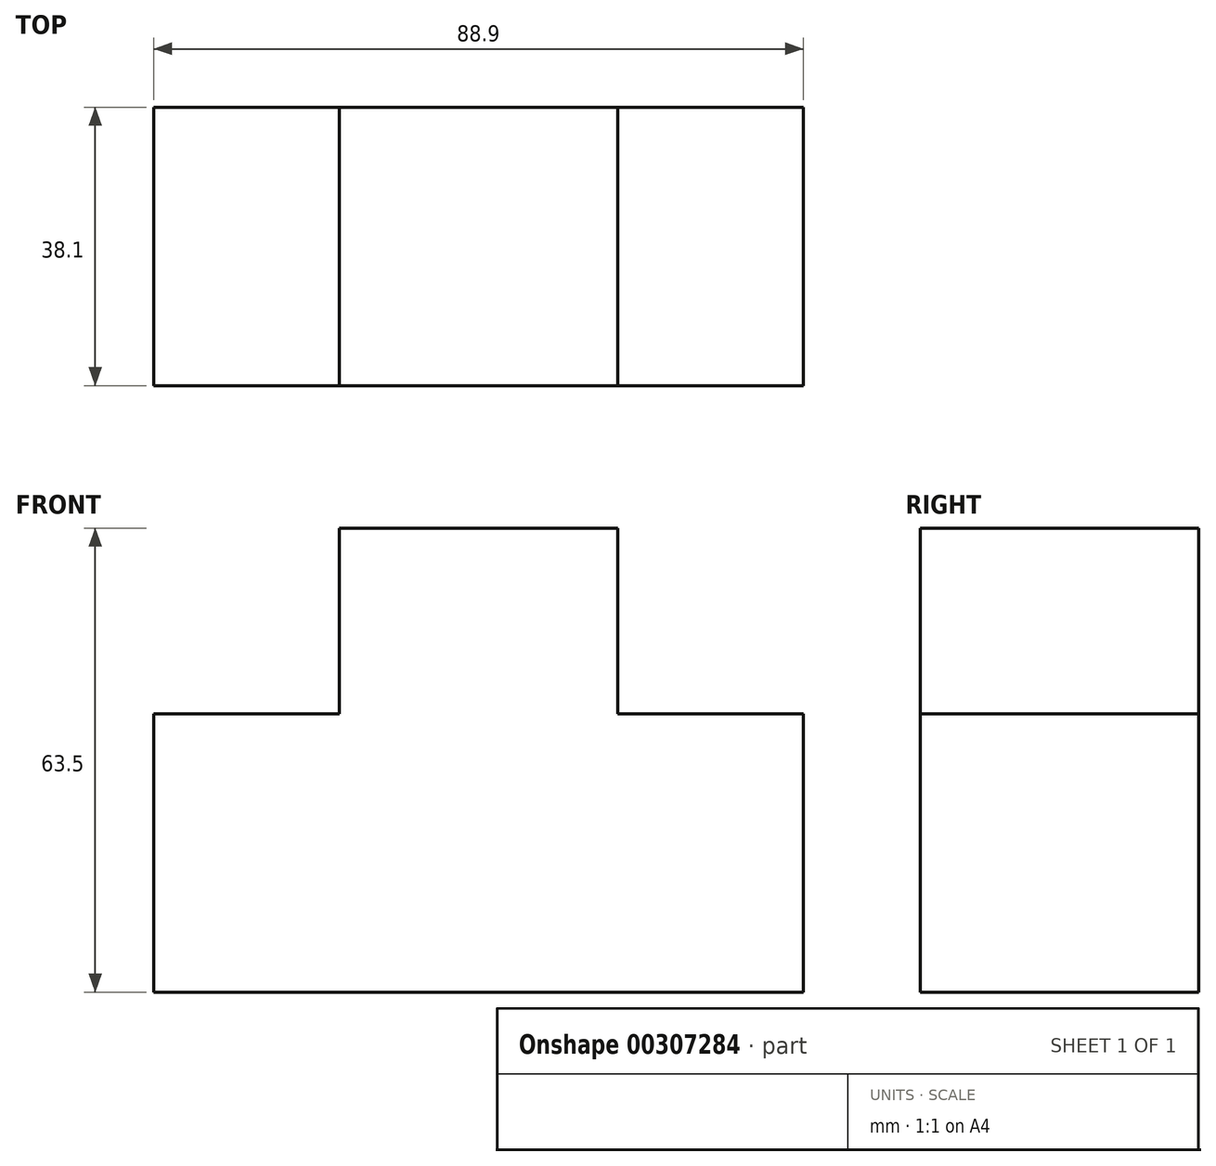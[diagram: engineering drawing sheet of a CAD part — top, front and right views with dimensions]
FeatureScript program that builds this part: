
annotation { "Feature Type Name" : "Feature", "Feature Type Description" : "" }
export const myFeature = defineFeature(function(context is Context, id is Id, definition is map)
    precondition{}
    {
        {
            var Q0;
            Q0=qCreatedBy(makeId("Front.planeOp"),FACE);
            var sketch = newSketch(context, id + "F0", { "sketchPlane" : qUnion([Q0])});
            skLineSegment(sketch, "E0", {"start": v(-42.03, -35.6) * mm, "end": v(46.87, -35.6) * mm});
            skLineSegment(sketch, "E1", {"start": v(46.87, -35.6) * mm, "end": v(46.87, 2.5) * mm});
            skLineSegment(sketch, "E2", {"start": v(46.87, 2.5) * mm, "end": v(21.47, 2.5) * mm});
            skLineSegment(sketch, "E3", {"start": v(21.47, 2.5) * mm, "end": v(21.47, 27.9) * mm});
            skLineSegment(sketch, "E4", {"start": v(21.47, 27.9) * mm, "end": v(-16.63, 27.9) * mm});
            skLineSegment(sketch, "E5", {"start": v(-16.63, 27.9) * mm, "end": v(-16.63, 2.5) * mm});
            skLineSegment(sketch, "E6", {"start": v(-16.63, 2.5) * mm, "end": v(-42.03, 2.5) * mm});
            skLineSegment(sketch, "E7", {"start": v(-42.03, 2.5) * mm, "end": v(-42.03, -35.6) * mm});
            skSolve(sketch);
        }
        {
            var Q0;
            Q0=makeQuery(id+"F0.imprint","IMPRINT",FACE,{"disambiguationData":[TD([[makeQuery(id+"F0.imprint","IMPRINT",EDGE,{"derivedFrom":sQuery(id+"F0.wireOp",EDGE,"E0")}),1.0]])]});
            extrude(context, id + "F1", {"entities" : qUnion([Q0]), "depth" : 38.1 * mm});
        }
    });
